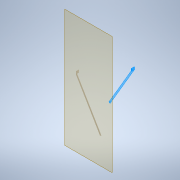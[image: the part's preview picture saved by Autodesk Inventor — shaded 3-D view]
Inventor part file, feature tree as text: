
AUTODESK INVENTOR PART (.ipt)
format: ipt  version: 2021 (Build 250183000, 183)  size: 161,792 bytes
history: native  units: mm
features: extrude x6, sketch x6, fillet x2, other x2, plane x1
ambient origin geometry x8: Origin, YZ Plane, XZ Plane, XY Plane, X Axis, Y Axis, Z Axis, Center Point
bodies: Solid1 (feature_tree)
feature tree (17):
  plane  "Work Plane1"
  extrude  "Extrusion1"  Depth=30.0mm
  extrude  "Extrusion2"  Depth=26.110126mm
  extrude  "Extrusion3"  Depth=6.0mm TaperAngle=0.0deg
  fillet  "Fillet1"  Radius=3.0mm
  extrude  "Extrusion4"  Depth=60.0mm TaperAngle=0.0deg
  fillet  "Fillet2"  Radius=6.0mm
  extrude  "Extrusion5"  Depth=2.0mm
  extrude  "Extrusion6"  Depth=10.0mm
  sketch  "Sketch1"  dims[d0=30.0mm d2=180.0mm]
  sketch  "Sketch2"  dims[d3=1350.0mm d4=26.110126mm]
  sketch  "Sketch3"  dims[d5=1060.0mm d6=6.0mm d7=0.0mm d8=3.0mm d9=0.0mm]
  sketch  "Sketch4"  dims[d10=3.0mm d11=60.0mm d12=0.0mm d13=6.0mm]
  sketch  "Sketch5"  dims[d14=90.0mm d15=45.0mm d16=0.0mm d17=0.0mm d18=2.0mm]
  sketch  "Sketch6"  dims[d19=51.8mm d20=32.2mm d21=10.0mm d22=10.0mm d23=0.0mm d24=10.0mm d25=15.0mm d26=27.5mm d27=10.0mm d28=0.0mm]
  other  "cover_final_assembly.iam"
  other  "wheelchair_box_extended:1"
